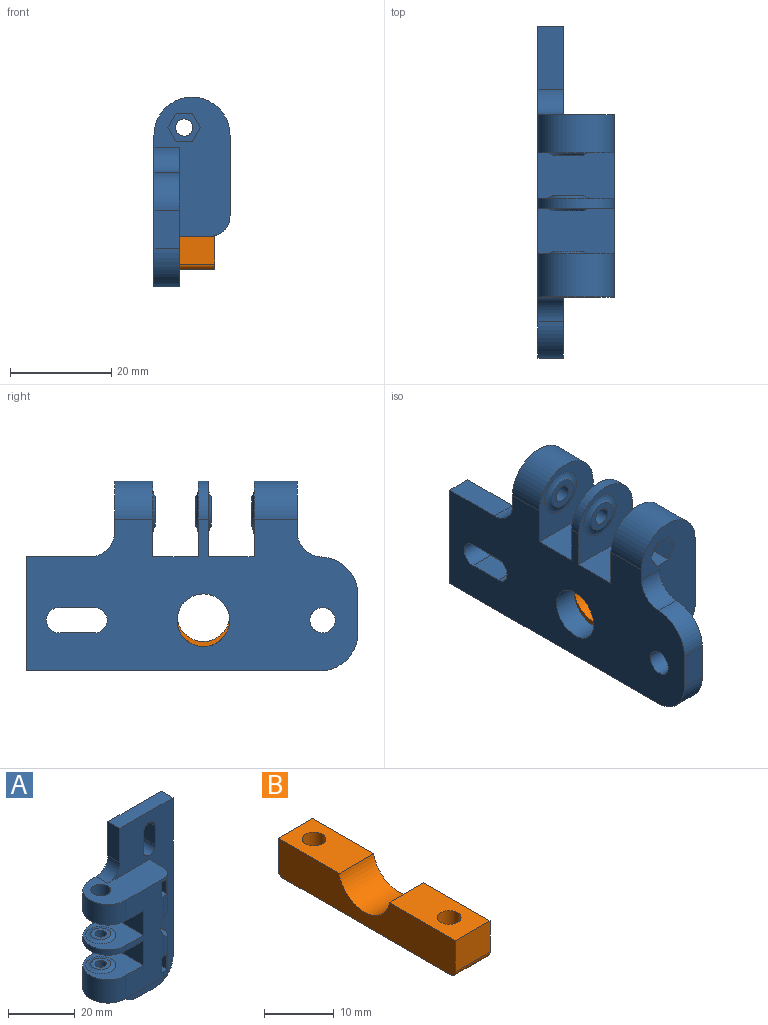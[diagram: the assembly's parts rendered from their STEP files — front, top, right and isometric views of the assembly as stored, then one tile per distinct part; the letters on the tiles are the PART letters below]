
ASSEMBLY  parts=2 mates=1
PART A: 70 faces, bbox 38.2x15.8x65.5 mm
  f0: plane 22.5x5mm, normal (0,0,1), area 112.5mm2, adj f1,f4,f20,f68
  f1: plane 65.5x27.5mm, normal (0,-1,0), area 893.5mm2, adj f0,f16,f17,f18,f20,f21,f22,f23
  f2: cylinder r=1.7mm len=3.4mm, axis (0,0,-1), area 32mm2, adj f52,f67
  f3: plane 36x15.96mm, normal (0,-1,0), area 423.8mm2, adj f6,f7,f8,f11,f12,f15,f21,f33
  f4: plane 65.5x29.96mm, normal (0,1,0), area 1435.4mm2, adj f0,f6,f7,f16,f17,f18,f20,f21
  f5: cylinder r=1.7mm len=3.4mm, axis (0,0,1), area 32mm2, adj f59,f61
  f6: plane 15x9mm, normal (-1,0,0), area 135mm2, adj f3,f4,f55,f58
  f7: plane 15x9mm, normal (-1,0,0), area 135mm2, adj f3,f4,f57,f60
  f8: plane 8.15x2.6mm, normal (0,0,1), area 21mm2, adj f3,f9,f38,f40,f50
  f9: plane 2.78x2.6mm, normal (0,-0.87,0.5), area 8.3mm2, adj f8,f10,f38,f40
  f10: plane 2.78x2.6mm, normal (0,-0.87,-0.5), area 8.3mm2, adj f9,f11,f38,f40
  f11: plane 8.15x2.6mm, normal (0,0,-1), area 21mm2, adj f3,f10,f38,f40,f50
  f12: plane 8.15x2.6mm, normal (0,0,-1), area 21mm2, adj f3,f13,f34,f39,f49
  f13: plane 2.78x2.6mm, normal (0,-0.87,-0.5), area 8.3mm2, adj f12,f14,f34,f39
  f14: plane 2.78x2.6mm, normal (0,-0.87,0.5), area 8.3mm2, adj f13,f15,f34,f39
  f15: plane 8.15x2.6mm, normal (0,0,1), area 21mm2, adj f3,f14,f34,f39,f49
  f16: plane 7.5x5mm, normal (0,0,-1), area 37.5mm2, adj f1,f4,f18,f69
  f17: cylinder r=2.5mm len=5mm, axis (0,-1,0), area 78.5mm2, adj f1,f4
  f18: cylinder r=7.5mm len=7.49mm, axis (0,-1,0), area 57.4mm2, adj f1,f4,f16,f54
  f19: cylinder r=1.7mm len=5mm, axis (0,0,1), area 53.4mm2, adj f32,f56
  f20: plane 12.5x5mm, normal (-1,0,0), area 62.5mm2, adj f0,f1,f4,f53
  f21: cylinder r=5.2mm len=15mm, axis (0,-1,0), area 319.7mm2, adj f1,f3,f4,f36,f37,f49,f50
  f22: cylinder r=2.5mm len=5mm, axis (0,-1,0), area 39.3mm2, adj f1,f4,f23,f24
  f23: plane 7x5mm, normal (1,0,0), area 35mm2, adj f1,f4,f22,f25
  f24: plane 7x5mm, normal (-1,0,0), area 35mm2, adj f1,f4,f22,f25
  f25: cylinder r=2.5mm len=5mm, axis (0,-1,0), area 39.3mm2, adj f1,f4,f23,f24
  f26: plane 4x2.78mm, normal (-0.5,-0.87,0), area 12.8mm2, adj f27,f31,f32,f33
  f27: plane 4x3.2mm, normal (-1,0,0), area 12.8mm2, adj f26,f28,f32,f33
  f28: plane 4x2.78mm, normal (-0.5,0.87,0), area 12.8mm2, adj f27,f29,f32,f33
  f29: plane 4x2.78mm, normal (0.5,0.87,0), area 12.8mm2, adj f28,f30,f32,f33
  f30: plane 4x3.2mm, normal (1,0,0), area 12.8mm2, adj f29,f31,f32,f33
  f31: plane 4x2.78mm, normal (0.5,-0.87,0), area 12.8mm2, adj f26,f30,f32,f33
  f32: plane 6.41x5.55mm, normal (0,0,-1), area 17.6mm2, adj f19,f26,f27,f28,f29,f30,f31
  f33: plane 27.46x15mm, normal (0,0,-1), area 270.3mm2, adj f1,f3,f4,f26,f27,f28,f29,f30
  f34: plane 9.75x5.55mm, normal (1,0,0), area 40.6mm2, adj f3,f12,f13,f14,f15,f45
  f35: plane 27.46x15mm, normal (0,0,1), area 268.6mm2, adj f1,f3,f4,f37,f48,f50,f53,f66
  f36: plane 13.3x6mm, normal (1,0,0), area 70.7mm2, adj f1,f21,f33,f42,f49
  f37: plane 12.3x6mm, normal (1,0,0), area 64.7mm2, adj f1,f21,f35,f41,f50
  f38: plane 9.75x5.55mm, normal (1,0,0), area 40.6mm2, adj f3,f8,f9,f10,f11,f43
  f39: plane 9.42x5.55mm, normal (-1,0,0), area 38.7mm2, adj f12,f13,f14,f15,f42,f49
  f40: plane 9.42x5.55mm, normal (-1,0,0), area 38.7mm2, adj f8,f9,f10,f11,f41,f50
  f41: cylinder r=1.7mm len=3.4mm, axis (1,0,0), area 25.6mm2, adj f37,f40
  f42: cylinder r=1.7mm len=3.4mm, axis (1,0,0), area 25.6mm2, adj f36,f39
  f43: cylinder r=1.7mm len=5mm, axis (1,0,0), area 53.4mm2, adj f38,f44
  f44: plane 3.4x3.4mm, normal (1,0,0), area 9.1mm2, adj f43
  f45: cylinder r=1.7mm len=5mm, axis (1,0,0), area 53.4mm2, adj f34,f46
  f46: plane 3.4x3.4mm, normal (1,0,0), area 9.1mm2, adj f45
  f47: cylinder r=7.5mm len=15mm, axis (0,0,1), area 200.3mm2, adj f3,f4,f33,f57
  f48: cylinder r=7.5mm len=15mm, axis (0,0,1), area 176.7mm2, adj f3,f4,f35,f55
  f49: cylinder r=4mm len=15.18mm, axis (0,0,-1), area 76.9mm2, adj f3,f12,f15,f21,f33,f36,f39
  f50: cylinder r=4mm len=14.18mm, axis (0,0,1), area 70.6mm2, adj f3,f8,f11,f21,f35,f37,f40
  f51: cylinder r=7.5mm len=15mm, axis (0,0,-1), area 47.1mm2, adj f3,f4,f58,f60
  f52: plane 6x6mm, normal (0,0,-1), area 19.2mm2, adj f2,f65
  f53: cylinder r=5mm len=5mm, axis (0,-1,0), area 39.3mm2, adj f1,f4,f20,f35
  f54: cylinder r=5mm len=5mm, axis (0,-1,0), area 38.3mm2, adj f1,f4,f18,f33
  f55: plane 15x14.96mm, normal (0,0,-1), area 136.7mm2, adj f3,f4,f6,f48,f65
  f56: plane 6x6mm, normal (0,0,1), area 19.2mm2, adj f19,f64
  f57: plane 15x14.96mm, normal (0,0,1), area 136.7mm2, adj f3,f4,f7,f47,f64
  f58: plane 15x14.96mm, normal (0,0,1), area 136.7mm2, adj f3,f4,f6,f51,f63
  f59: plane 6x6mm, normal (0,0,1), area 19.2mm2, adj f5,f63
  f60: plane 15x14.96mm, normal (0,0,-1), area 136.7mm2, adj f3,f4,f7,f51,f62
  f61: plane 6x6mm, normal (0,0,-1), area 19.2mm2, adj f5,f62
  f62: torus R=4.5mm, axis (0,0,1), area 37.6mm2, adj f60,f61
  f63: torus R=4.5mm, axis (0,0,1), area 37.6mm2, adj f58,f59
  f64: torus R=4.5mm, axis (0,0,1), area 37.6mm2, adj f56,f57
  f65: torus R=4.5mm, axis (0,0,1), area 37.6mm2, adj f52,f55
  f66: cylinder r=3mm len=6mm, axis (0,0,1), area 94.2mm2, adj f35,f67
  f67: plane 6x6mm, normal (0,0,1), area 19.2mm2, adj f2,f66
  f68: plane 58x5mm, normal (1,0,0), area 290mm2, adj f0,f1,f4,f69
  f69: cylinder r=7.5mm len=7.5mm, axis (0,1,0), area 58.9mm2, adj f1,f4,f16,f68
PART B: 12 faces, bbox 7x36x6.5 mm
  f0: plane 36x6.5mm, normal (1,0,0), area 201.4mm2, adj f1,f2,f4,f5,f6,f9,f10,f11
  f1: plane 7x5.5mm, normal (0,-1,0), area 38.5mm2, adj f0,f3,f6,f11
  f2: plane 7x5.5mm, normal (0,1,0), area 38.5mm2, adj f0,f3,f5,f10
  f3: plane 36x6.5mm, normal (-1,0,0), area 201.4mm2, adj f1,f2,f4,f5,f6,f9,f10,f11
  f4: cylinder r=5.2mm len=10.21mm, axis (1,0,0), area 100.3mm2, adj f0,f3,f5,f6
  f5: plane 12.4x7mm, normal (0,0,1), area 77.7mm2, adj f0,f2,f3,f4,f8
  f6: plane 13.4x7mm, normal (0,0,1), area 84.7mm2, adj f0,f1,f3,f4,f7
  f7: cylinder r=1.7mm len=6.5mm, axis (0,0,-1), area 69.4mm2, adj f6,f9
  f8: cylinder r=1.7mm len=6.5mm, axis (0,0,-1), area 69.4mm2, adj f5,f9
  f9: plane 34x7mm, normal (0,0,-1), area 219.8mm2, adj f0,f3,f7,f8,f10,f11
  f10: cylinder r=1mm len=7mm, axis (-1,0,0), area 11mm2, adj f0,f2,f3,f9
  f11: cylinder r=1mm len=7mm, axis (1,0,0), area 11mm2, adj f0,f1,f3,f9
PLACE A rot(axis=(-0.58,0.58,0.58),120deg) t=(-2.06,5.04,-39.21)mm
PLACE B t=(0.39,0.79,-58.21)mm
MATE fastened A.f41 <-> B.f8  axis (0,0,-1) through (0.39,15.01,-46.71)mm
